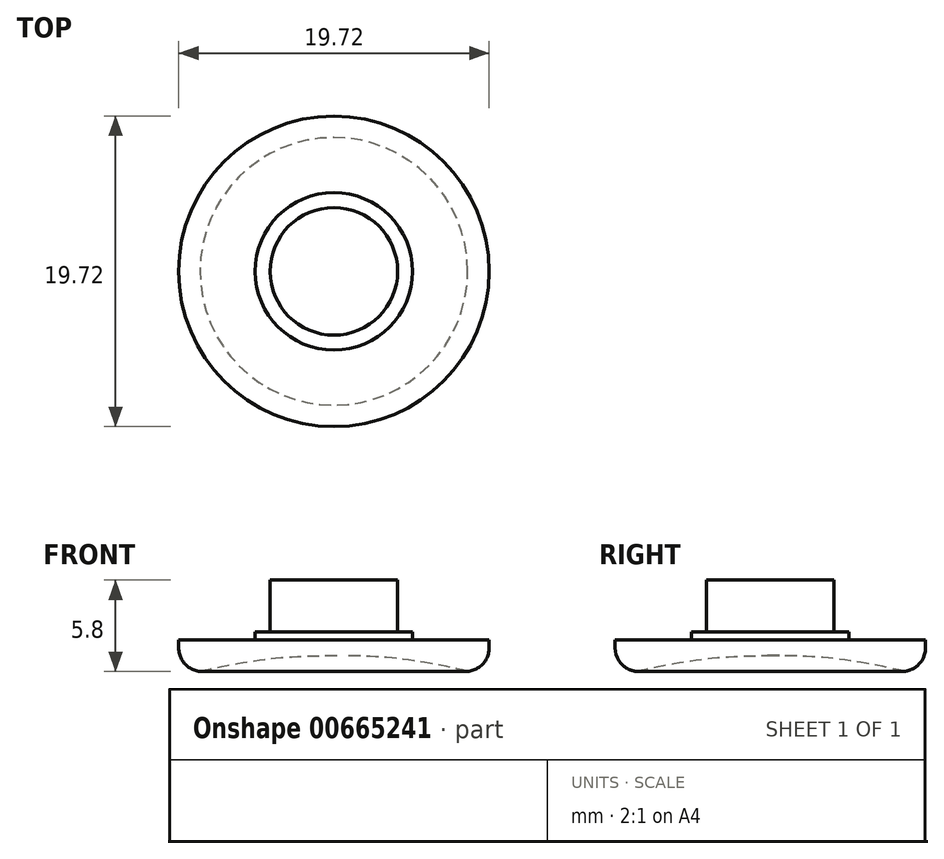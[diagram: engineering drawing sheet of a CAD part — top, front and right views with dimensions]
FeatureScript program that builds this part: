
annotation { "Feature Type Name" : "Feature", "Feature Type Description" : "" }
export const myFeature = defineFeature(function(context is Context, id is Id, definition is map)
    precondition{}
    {
        {
            var Q0;
            Q0=qCreatedBy(makeId("Top.planeOp"),FACE);
            var sketch = newSketch(context, id + "F0", { "sketchPlane" : qUnion([Q0])});
            skCircle(sketch, "E0", {"center": v(0, 0) * mm, "radius": 9.86 * mm});
            skSolve(sketch);
        }
        {
            var Q0;
            Q0=qSketchRegion(id+"F0",true);
            extrude(context, id + "F1", {"entities" : qUnion([Q0]), "depth" : 2 * mm, "offsetDistance" : 25 * mm});
        }
        {
            var Q0;
            Q0=makeQuery(id+"F1.opExtrude","CAP_FACE",FACE,{"disambiguationData":[OSD([sQuery(id+"F0.wireOp",EDGE,"E0")])],"isStart":false});
            var sketch = newSketch(context, id + "F2", { "sketchPlane" : qUnion([Q0])});
            skCircle(sketch, "E1", {"center": v(0, 0) * mm, "radius": 5 * mm});
            skSolve(sketch);
        }
        {
            var Q0;
            Q0=qSketchRegion(id+"F2",true);
            extrude(context, id + "F3", {"entities" : qUnion([Q0]), "operationType" : NewBodyOperationType.ADD, "depth" : .5 * mm, "offsetDistance" : 25 * mm});
        }
        {
            var Q0;
            Q0=makeQuery(id+"F3.opExtrude","CAP_FACE",FACE,{"disambiguationData":[OSD([sQuery(id+"F2.wireOp",EDGE,"E1")])],"isStart":false});
            var sketch = newSketch(context, id + "F4", { "sketchPlane" : qUnion([Q0])});
            skCircle(sketch, "E2", {"center": v(0, 0) * mm, "radius": 4.05 * mm});
            skSolve(sketch);
        }
        {
            var Q0;
            Q0=qSketchRegion(id+"F4",true);
            extrude(context, id + "F5", {"entities" : qUnion([Q0]), "operationType" : NewBodyOperationType.ADD, "depth" : 3.3 * mm, "offsetDistance" : 25 * mm});
        }
        {
            var Q0;
            Q0=makeQuery(id+"F1.opExtrude","CAP_FACE",FACE,{"disambiguationData":[OSD([sQuery(id+"F0.wireOp",EDGE,"E0")])],"isStart":true});
            var sketch = newSketch(context, id + "F6", { "sketchPlane" : qUnion([Q0])});
            skCircle(sketch, "E3", {"center": v(0, 0) * mm, "radius": 8.5 * mm});
            skSolve(sketch);
        }
        {
            var Q0;
            Q0=qSketchRegion(id+"F6",true);
            extrude(context, id + "F7", {"entities" : qUnion([Q0]), "operationType" : NewBodyOperationType.REMOVE, "oppositeDirection" : true, "depth" : 1 * mm, "offsetDistance" : 25 * mm});
        }
        {
            var Q0;
            Q0=makeQuery(id+"F7.boolean.opBoolean","COPY",EDGE,{"derivedFrom":makeQuery(id+"F7.opExtrude","CAP_EDGE",EDGE,{"disambiguationData":[OSD([sQuery(id+"F6.wireOp",EDGE,"E3")])],"isStart":false})});
            fillet(context, id + "F8", {"entities" : qUnion([Q0]), "radius" : 32 * mm, "tangentPropagation" : true, "allowEdgeOverflow" : false});
        }
        {
            var Q0;
            Q0=makeQuery(id+"F1.opExtrude","CAP_EDGE",EDGE,{"disambiguationData":[OSD([sQuery(id+"F0.wireOp",EDGE,"E0")])],"isStart":true});
            fillet(context, id + "F9", {"entities" : qUnion([Q0]), "radius" : 1.5 * mm, "tangentPropagation" : true, "allowEdgeOverflow" : false});
        }
    });
